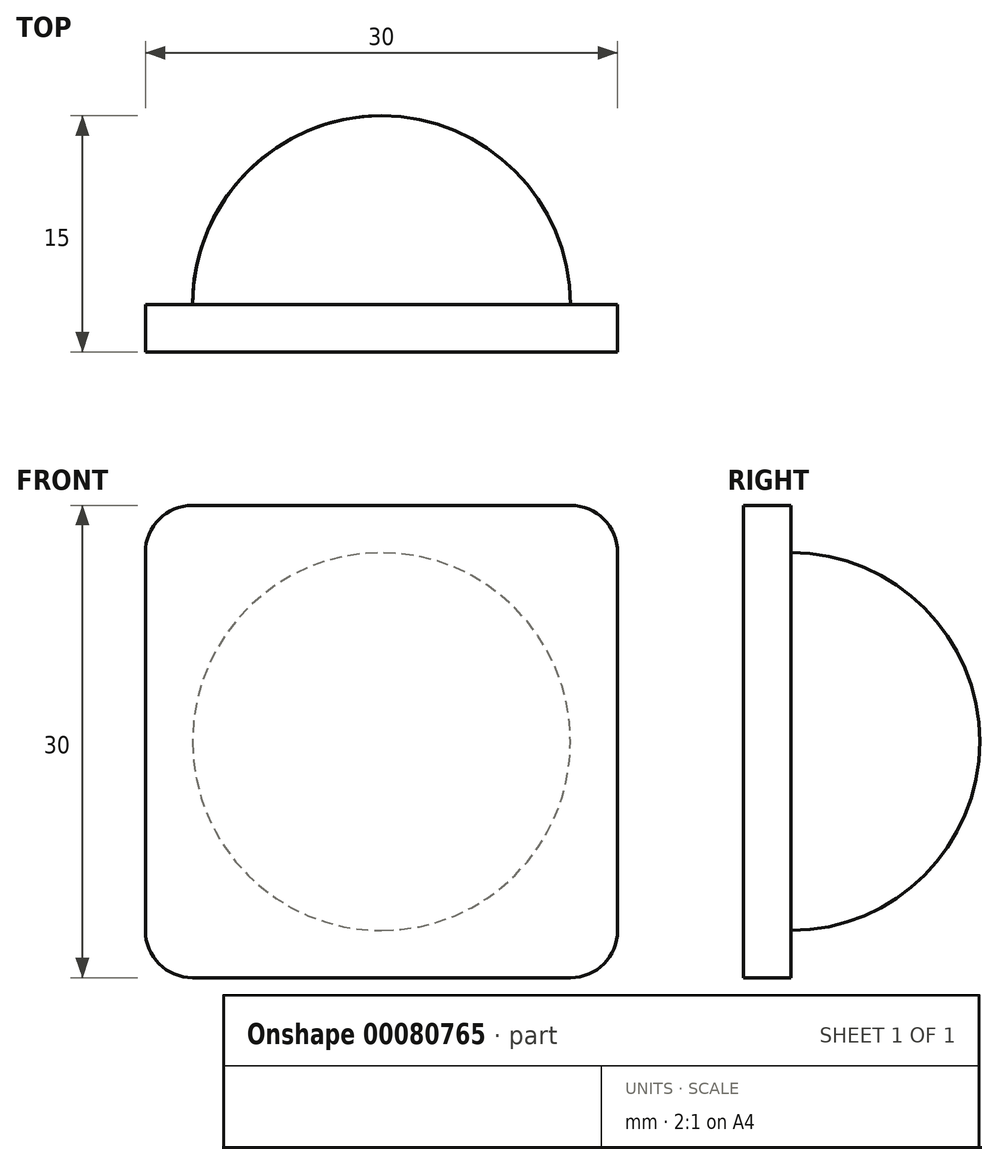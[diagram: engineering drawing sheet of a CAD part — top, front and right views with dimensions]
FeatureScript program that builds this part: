
annotation { "Feature Type Name" : "Feature", "Feature Type Description" : "" }
export const myFeature = defineFeature(function(context is Context, id is Id, definition is map)
    precondition{}
    {
        {
            var Q0;
            Q0=qCreatedBy(makeId("Top.planeOp"),FACE);
            var sketch = newSketch(context, id + "F0", { "sketchPlane" : qUnion([Q0])});
            skLineSegment(sketch, "E0", {"start": v(0, 0) * mm, "end": v(-12, 0) * mm});
            skLineSegment(sketch, "E1", {"start": v(0, 0) * mm, "end": v(0, 12) * mm});
            skArc(sketch, "E2", {"start": v(0, 12) * mm, "mid": v(-8.49, 8.49) * mm, "end": v(-12, 0) * mm});
            skSolve(sketch);
        }
        {
            var Q0;
            Q0=makeQuery(id+"F0.imprint","IMPRINT",FACE,{"disambiguationData":[TD([[makeQuery(id+"F0.imprint","IMPRINT",EDGE,{"derivedFrom":sQuery(id+"F0.wireOp",EDGE,"E0")}),-1.0]])]});
            var Q1;
            Q1=sQuery(id+"F0.wireOp",EDGE,"E1");
            revolve(context, id + "F1", {"entities" : qUnion([Q0]), "axis" : qUnion([Q1]), "revolveType" : RevolveType.FULL});
        }
        {
            var Q0;
            Q0=qCreatedBy(makeId("Front.planeOp"),FACE);
            var sketch = newSketch(context, id + "F2", { "sketchPlane" : qUnion([Q0])});
            skLineSegment(sketch, "E3", {"start": v(0, 0) * mm, "end": v(14.95, 0) * mm});
            skLineSegment(sketch, "E4", {"start": v(0, 0) * mm, "end": v(0, -15) * mm});
            skLineSegment(sketch, "E5", {"start": v(0, 0) * mm, "end": v(-15, 0) * mm});
            skLineSegment(sketch, "E6", {"start": v(0, 0) * mm, "end": v(0, 14.95) * mm});
            skLineSegment(sketch, "E7", {"start": v(0, -15) * mm, "end": v(-15, -15) * mm});
            skLineSegment(sketch, "E8", {"start": v(0, -15) * mm, "end": v(15, -15) * mm});
            skLineSegment(sketch, "E9", {"start": v(-15, -15) * mm, "end": v(-15, 15) * mm});
            skLineSegment(sketch, "E10", {"start": v(-15, 15) * mm, "end": v(15, 15) * mm});
            skLineSegment(sketch, "E11", {"start": v(15, -15) * mm, "end": v(15, 15) * mm});
            skLineSegment(sketch, "E12.MirrorCS", {"start": v(0, 0) * mm, "end": v(15, 0) * mm});
            skSolve(sketch);
        }
        {
            var Q0;
            Q0=makeQuery(id+"F2.imprint","IMPRINT",FACE,{"disambiguationData":[TD([[makeQuery(id+"F2.imprint","IMPRINT",EDGE,{"derivedFrom":sQuery(id+"F2.wireOp",EDGE,"E4")}),-1.0]])]});
            var Q1;
            {var subQ4=sQuery(id+"F2.wireOp",EDGE,"E4");Q1=makeQuery(id+"F2.imprint","IMPRINT",FACE,{"disambiguationData":[TD([[makeQuery(id+"F2.imprint","IMPRINT",EDGE,{"derivedFrom":subQ4}),1.0]])]});}
            var Q2;
            {var subQ2=sQuery(id+"F2.wireOp",EDGE,"E5");Q2=makeQuery(id+"F2.imprint","IMPRINT",FACE,{"disambiguationData":[TD([[makeQuery(id+"F2.imprint","IMPRINT",EDGE,{"derivedFrom":subQ2}),-1.0]])]});}
            extrude(context, id + "F3", {"entities" : qUnion([Q0, Q1, Q2]), "operationType" : NewBodyOperationType.ADD, "depth" : 3 * mm});
        }
        {
            var Q0;
            Q0=makeQuery(id+"F3.opExtrude","SWEPT_EDGE",EDGE,{"disambiguationData":[OSD([sQuery(id+"F2.wireOp",EDGE,"E10"),sQuery(id+"F2.wireOp",EDGE,"E11")])]});
            var Q1;
            Q1=makeQuery(id+"F3.opExtrude","SWEPT_EDGE",EDGE,{"disambiguationData":[OSD([sQuery(id+"F2.wireOp",EDGE,"E8"),sQuery(id+"F2.wireOp",EDGE,"E11")])]});
            var Q2;
            Q2=makeQuery(id+"F3.opExtrude","SWEPT_EDGE",EDGE,{"disambiguationData":[OSD([sQuery(id+"F2.wireOp",EDGE,"E7"),sQuery(id+"F2.wireOp",EDGE,"E9")])]});
            var Q3;
            Q3=makeQuery(id+"F3.opExtrude","SWEPT_EDGE",EDGE,{"disambiguationData":[OSD([sQuery(id+"F2.wireOp",EDGE,"E9"),sQuery(id+"F2.wireOp",EDGE,"E10")])]});
            var Q4;
            Q4=makeQuery(id+"F1.opRevolve","SWEPT_EDGE",EDGE,{"disambiguationData":[OSD([sQuery(id+"F0.wireOp",EDGE,"E0"),sQuery(id+"F0.wireOp",EDGE,"E2")])]});
            fillet(context, id + "F4", {"entities" : qUnion([Q0, Q1, Q2, Q3, Q4]), "radius" : 3 * mm, "tangentPropagation" : true, "allowEdgeOverflow" : false});
        }
    });
